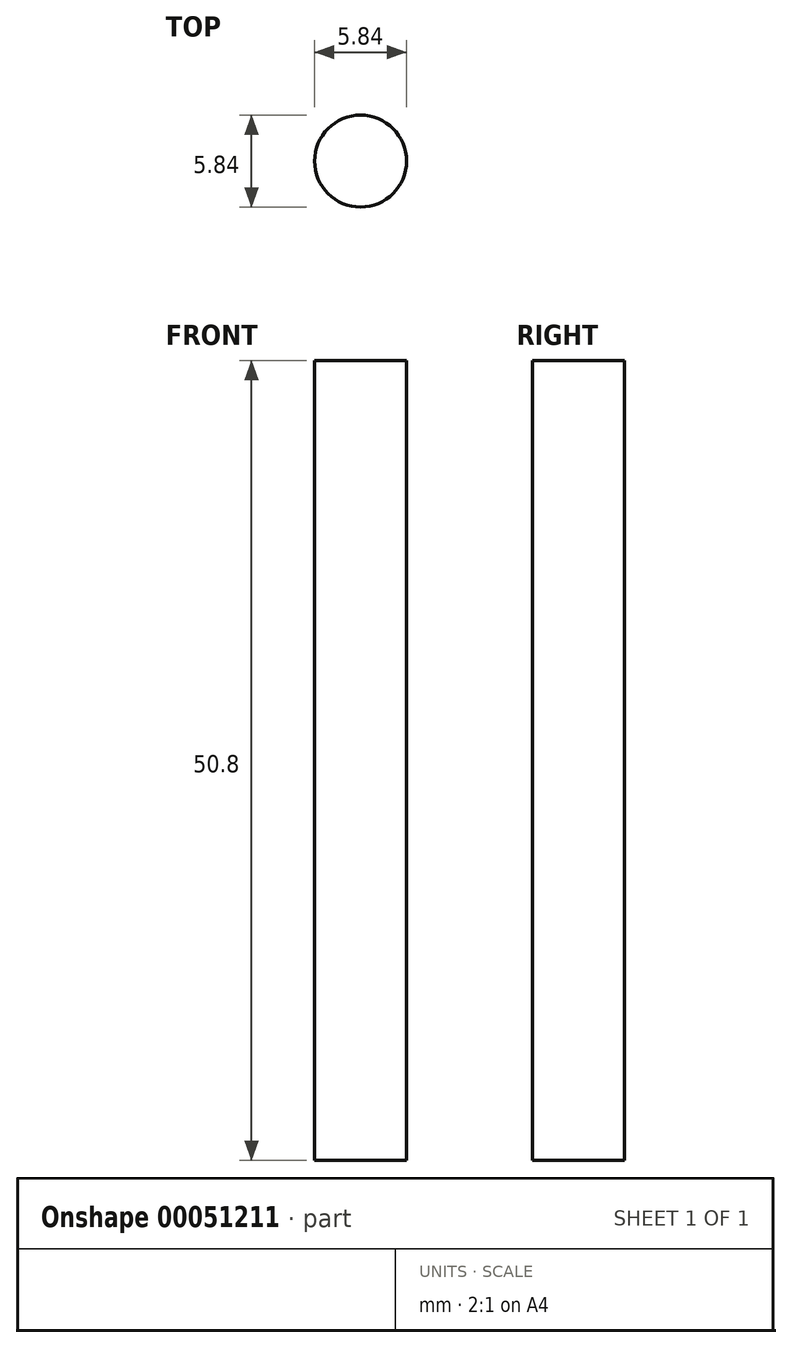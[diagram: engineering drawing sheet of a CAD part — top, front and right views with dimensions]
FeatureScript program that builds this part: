
annotation { "Feature Type Name" : "Feature", "Feature Type Description" : "" }
export const myFeature = defineFeature(function(context is Context, id is Id, definition is map)
    precondition{}
    {
        {
            var Q0;
            Q0=qCreatedBy(makeId("Top.planeOp"),FACE);
            var sketch = newSketch(context, id + "F0", { "sketchPlane" : qUnion([Q0])});
            skCircle(sketch, "E0", {"center": v(0, 0) * mm, "radius": 2.92 * mm});
            skSolve(sketch);
        }
        {
            var Q0;
            Q0=qSketchRegion(id+"F0",true);
            extrude(context, id + "F1", {"entities" : qUnion([Q0]), "depth" : 50.8 * mm});
        }
    });
